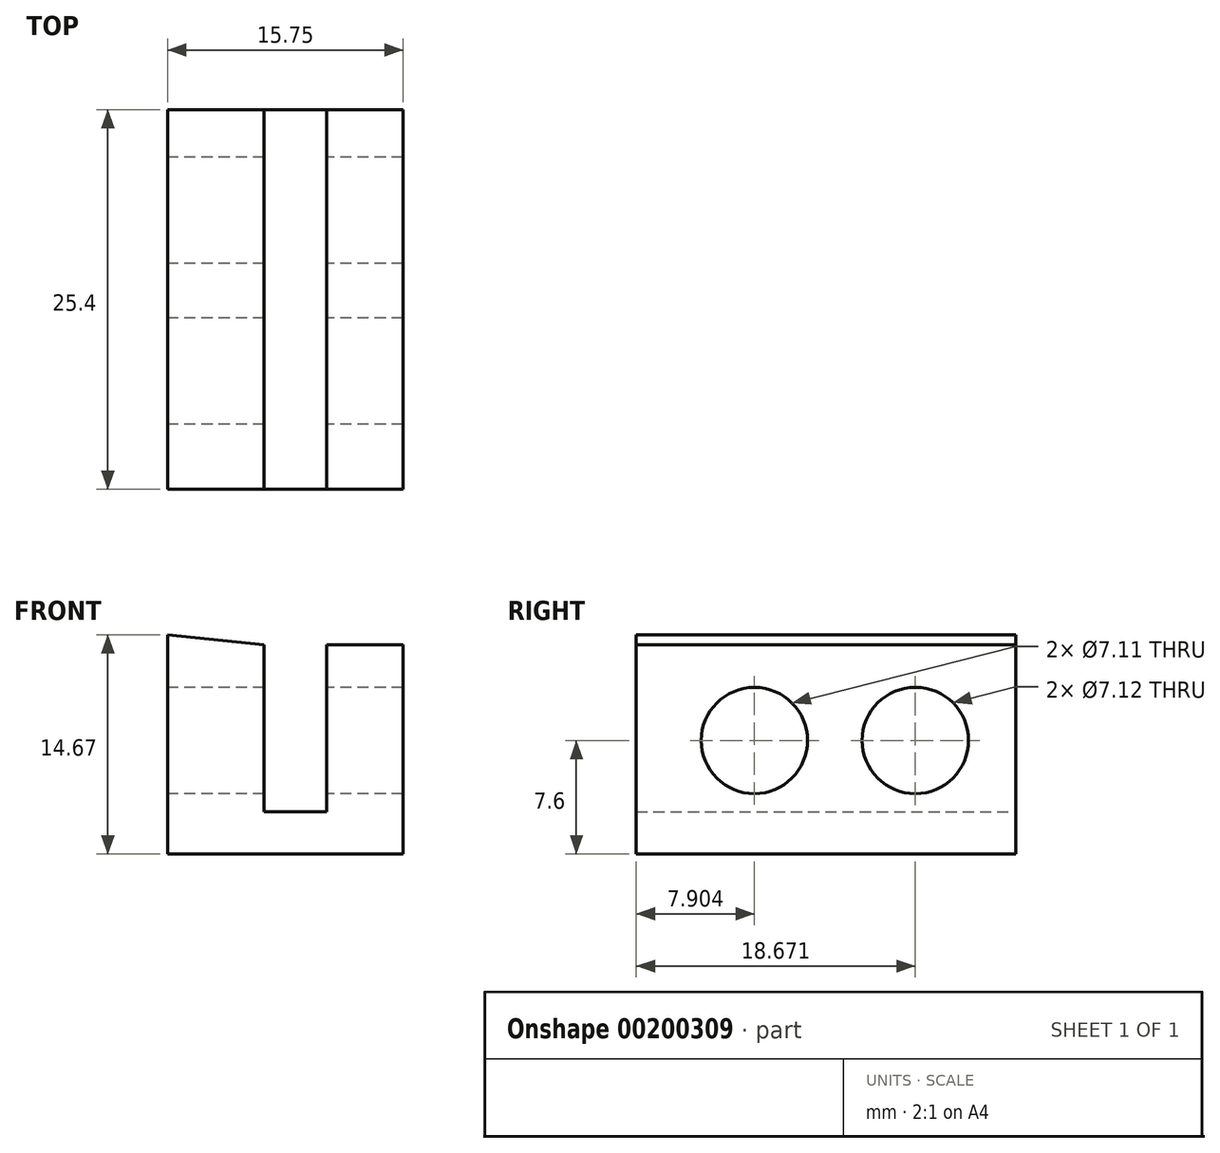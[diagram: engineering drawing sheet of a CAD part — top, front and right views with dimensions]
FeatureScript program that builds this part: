
annotation { "Feature Type Name" : "Feature", "Feature Type Description" : "" }
export const myFeature = defineFeature(function(context is Context, id is Id, definition is map)
    precondition{}
    {
        {
            var Q0;
            Q0=qCreatedBy(makeId("Front.planeOp"),FACE);
            var sketch = newSketch(context, id + "F0", { "sketchPlane" : qUnion([Q0])});
            skLineSegment(sketch, "E0", {"start": v(7.13, 7.07) * mm, "end": v(7.13, -7.6) * mm});
            skLineSegment(sketch, "E1", {"start": v(7.13, -7.6) * mm, "end": v(22.88, -7.6) * mm});
            skLineSegment(sketch, "E2", {"start": v(22.88, -7.6) * mm, "end": v(22.88, 6.4) * mm});
            skLineSegment(sketch, "E3", {"start": v(22.88, 6.4) * mm, "end": v(17.77, 6.4) * mm});
            skLineSegment(sketch, "E4", {"start": v(17.77, 6.4) * mm, "end": v(17.77, -4.78) * mm});
            skLineSegment(sketch, "E5", {"start": v(17.77, -4.78) * mm, "end": v(13.6, -4.78) * mm});
            skLineSegment(sketch, "E6", {"start": v(13.6, -4.78) * mm, "end": v(13.6, 6.4) * mm});
            skLineSegment(sketch, "E7", {"start": v(13.6, 6.4) * mm, "end": v(7.13, 7.07) * mm});
            skSolve(sketch);
        }
        {
            var Q0;
            Q0 = qSketchRegion(id + "F0", true);
            extrude(context, id + "F1", {"entities" : qUnion([Q0]), "depth" : 25.4 * mm});
        }
        {
            var Q0;
            Q0=makeQuery(id+"F1.opExtrude","SWEPT_FACE",FACE,{"disambiguationData":[OSD([sQuery(id+"F0.wireOp",EDGE,"E0")])]});
            var sketch = newSketch(context, id + "F2", { "sketchPlane" : qUnion([Q0])});
            skCircle(sketch, "E8", {"center": v(6.73, 0) * mm, "radius": 3.56 * mm});
            skCircle(sketch, "E9", {"center": v(17.5, 0) * mm, "radius": 3.56 * mm});
            skSolve(sketch);
        }
        {
            var Q0;
            Q0 = qSketchRegion(id + "F2", true);
            extrude(context, id + "F3", {"entities" : qUnion([Q0]), "operationType" : NewBodyOperationType.REMOVE, "oppositeDirection" : true, "depth" : 25.4 * mm});
        }
    });
